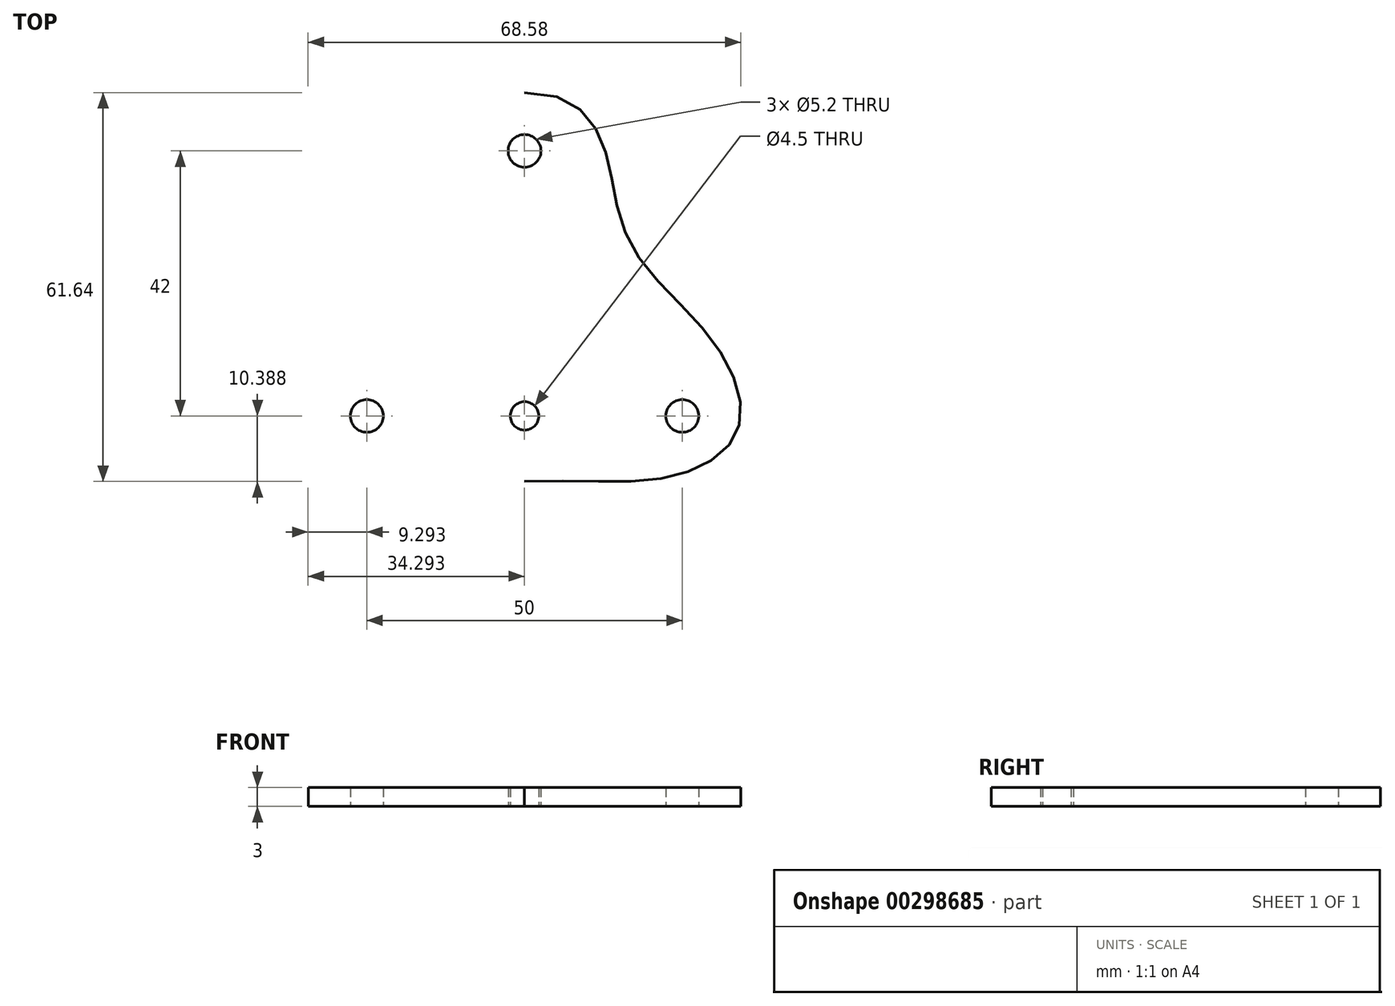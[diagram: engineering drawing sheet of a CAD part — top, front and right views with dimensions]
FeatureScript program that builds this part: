
annotation { "Feature Type Name" : "Feature", "Feature Type Description" : "" }
export const myFeature = defineFeature(function(context is Context, id is Id, definition is map)
    precondition{}
    {
        {
            var Q0;
            Q0=qCreatedBy(makeId("Top.planeOp"),FACE);
            var sketch = newSketch(context, id + "F0", { "sketchPlane" : qUnion([Q0])});
            skCircle(sketch, "E0", {"center": v(12.46, 4.43) * mm, "radius": 2.6 * mm});
            skCircle(sketch, "E1", {"center": v(37.46, -37.57) * mm, "radius": 2.6 * mm});
            skCircle(sketch, "E2", {"center": v(-12.54, -37.57) * mm, "radius": 2.6 * mm});
            skLineSegment(sketch, "E3", {"start": v(12.46, 5.9) * mm, "end": v(12.46, -52.9) * mm, "construction": true});
            skFitSpline(sketch, "E4", {"points": [v(12.46, 13.68) * mm, v(24.74, 5.9) * mm, v(29.06, -9.94) * mm, v(42.45, -25.92) * mm, v(46.34, -39.46) * mm, v(36.7, -46.95) * mm, v(12.46, -47.95) * mm], "startDerivative": vector(135.1, 3) * mm, "endDerivative": vector(-145.53, -5.3) * mm});
            skFitSpline(sketch, "E5.MirrorCS", {"points": [v(12.46, 13.68) * mm, v(0.18, 5.9) * mm, v(-4.14, -9.94) * mm, v(-17.53, -25.92) * mm, v(-21.42, -39.46) * mm, v(-11.77, -46.95) * mm, v(12.46, -47.95) * mm], "startDerivative": vector(-135.1, 3) * mm, "endDerivative": vector(145.53, -5.3) * mm});
            skCircle(sketch, "E6", {"center": v(12.46, -37.57) * mm, "radius": 2.25 * mm});
            skSolve(sketch);
        }
        {
            var Q0;
            Q0=qSketchRegion(id+"F0",true);
            extrude(context, id + "F1", {"entities" : qUnion([Q0]), "depth" : 3 * mm});
        }
        {
            var Q0;
            Q0=makeQuery(id+"F1.opExtrude","CAP_FACE",FACE,{"disambiguationData":[OSD([sQuery(id+"F0.wireOp",EDGE,"E0"),sQuery(id+"F0.wireOp",EDGE,"E1"),sQuery(id+"F0.wireOp",EDGE,"E2"),sQuery(id+"F0.wireOp",EDGE,"dVXcSlPP-XXvO-6OeD-0uax-jvAfKnYlGIrO"),sQuery(id+"F0.wireOp",EDGE,"gXV22Ezd-BxGV-p7MN-5mEq-ep9CFymhMpRn"),sQuery(id+"F0.wireOp",EDGE,"WmkqfEUB-IWB8-ESqq-jCjN-kpA6IxgFtCK6"),sQuery(id+"F0.wireOp",EDGE,"E4"),sQuery(id+"F0.wireOp",EDGE,"E5.MirrorCS")])],"isStart":false});
            var sketch = newSketch(context, id + "F2", { "sketchPlane" : qUnion([Q0])});
            skCircle(sketch, "E7", {"center": v(13.2, -12.8) * mm, "radius": 8.8 * mm});
            skCircle(sketch, "E8", {"center": v(2.84, -28.45) * mm, "radius": 6.03 * mm});
            skCircle(sketch, "E9", {"center": v(22.14, -29.31) * mm, "radius": 6.13 * mm});
            skSolve(sketch);
        }
    });
